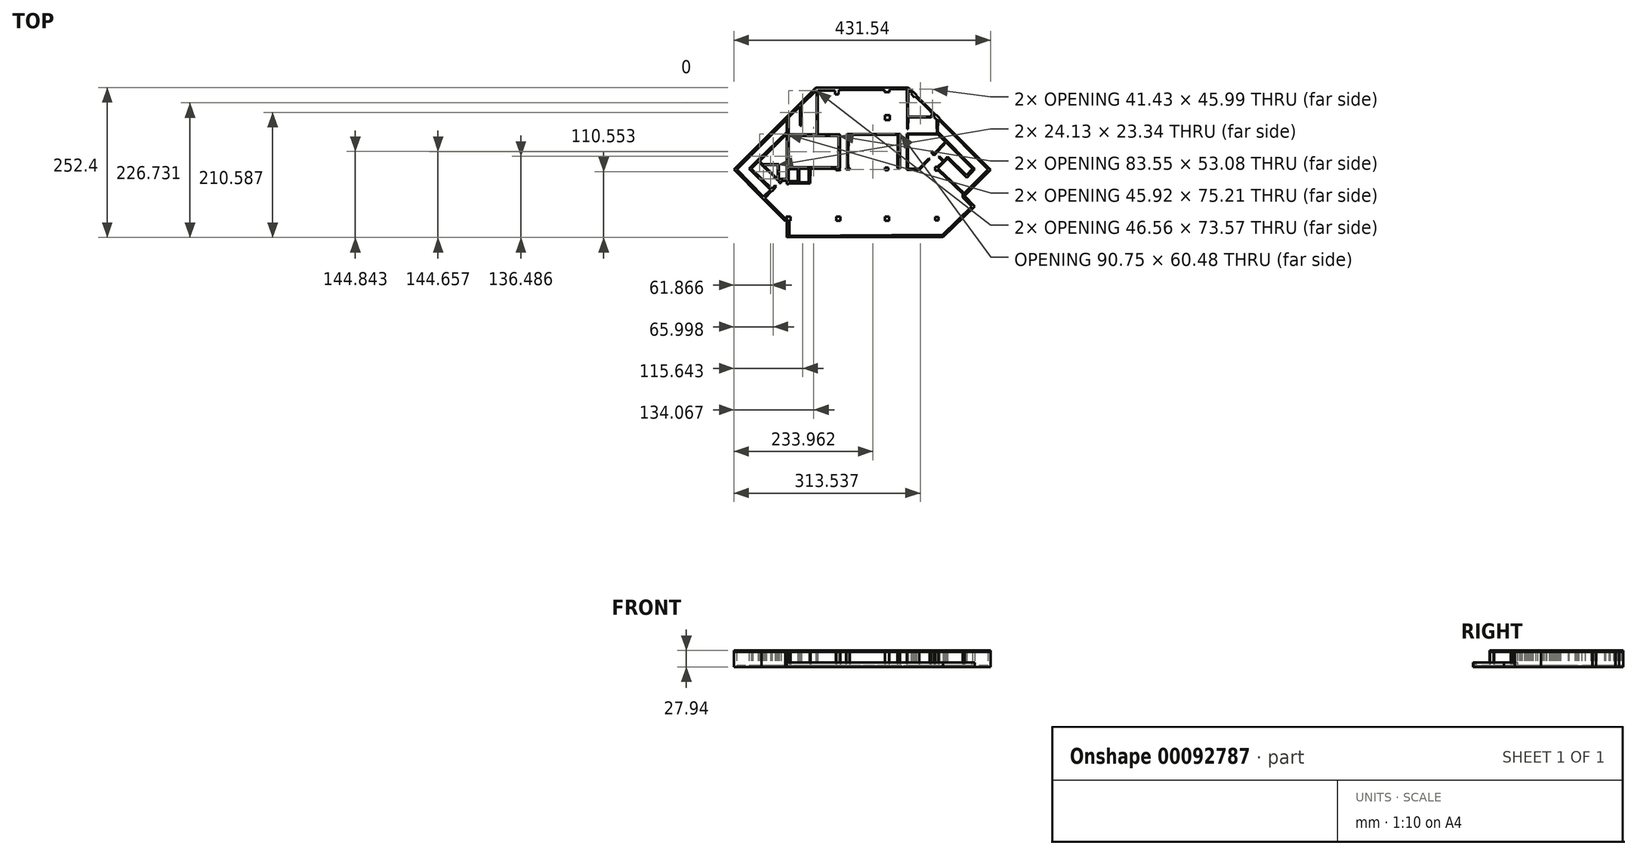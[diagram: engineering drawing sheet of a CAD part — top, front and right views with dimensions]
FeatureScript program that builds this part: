
annotation { "Feature Type Name" : "Feature", "Feature Type Description" : "" }
export const myFeature = defineFeature(function(context is Context, id is Id, definition is map)
    precondition{}
    {
        {
            var Q0;
            Q0=qCreatedBy(makeId("Top.planeOp"),FACE);
            var sketch = newSketch(context, id + "F0", { "sketchPlane" : qUnion([Q0])});
            skFitSpline(sketch, "E0", {"points": [v(-174.44, 1.7) * mm, v(-159.98, -12.91) * mm, v(-156, -16.03) * mm, v(-141.6, -30.7) * mm]});
            skLineSegment(sketch, "E1", {"start": v(-78.22, 126.2) * mm, "end": v(-126.81, 77.3) * mm});
            skLineSegment(sketch, "E2", {"start": v(-126.81, 77.3) * mm, "end": v(-126.8, 72.34) * mm});
            skLineSegment(sketch, "E3", {"start": v(-126.8, 72.34) * mm, "end": v(-126.81, 51.33) * mm});
            skLineSegment(sketch, "E4", {"start": v(-126.81, 51.33) * mm, "end": v(-175, 4.76) * mm});
            skLineSegment(sketch, "E5", {"start": v(-175, 4.76) * mm, "end": v(-190.1, -10.54) * mm});
            skLineSegment(sketch, "E6", {"start": v(-190.1, -10.54) * mm, "end": v(-154.22, -45.73) * mm});
            skLineSegment(sketch, "E7", {"start": v(-154.22, -45.73) * mm, "end": v(-166.17, -57.54) * mm});
            skLineSegment(sketch, "E8", {"start": v(-166.17, -57.54) * mm, "end": v(-211.21, -11.79) * mm});
            skLineSegment(sketch, "E9", {"start": v(-211.21, -11.79) * mm, "end": v(-186.84, 13.8) * mm});
            skLineSegment(sketch, "E10", {"start": v(-186.84, 13.8) * mm, "end": v(-184.08, 15.95) * mm});
            skLineSegment(sketch, "E11", {"start": v(-184.08, 15.95) * mm, "end": v(-126.84, 72.68) * mm});
            skLineSegment(sketch, "E12", {"start": v(-126.84, 72.68) * mm, "end": v(-126.9, 77.1) * mm});
            skLineSegment(sketch, "E13", {"start": v(-126.9, 77.1) * mm, "end": v(-215.77, -11.79) * mm});
            skLineSegment(sketch, "E14", {"start": v(-215.77, -11.79) * mm, "end": v(-169.23, -58.33) * mm});
            skLineSegment(sketch, "E15", {"start": v(-169.23, -58.33) * mm, "end": v(-169.38, -58.47) * mm});
            skLineSegment(sketch, "E16", {"start": v(-169.38, -58.47) * mm, "end": v(-129.39, -98.47) * mm});
            skLineSegment(sketch, "E17", {"start": v(-129.39, -98.47) * mm, "end": v(-126.88, -97.8) * mm});
            skLineSegment(sketch, "E18", {"start": v(-126.88, -97.8) * mm, "end": v(-126.88, -93.73) * mm});
            skLineSegment(sketch, "E19", {"start": v(-126.88, -93.73) * mm, "end": v(-130.37, -93.73) * mm});
            skLineSegment(sketch, "E20", {"start": v(-130.37, -93.73) * mm, "end": v(-161.45, -62.66) * mm});
            skLineSegment(sketch, "E21", {"start": v(-161.45, -62.66) * mm, "end": v(-163.98, -59.75) * mm});
            skLineSegment(sketch, "E22", {"start": v(-163.98, -59.75) * mm, "end": v(-152.34, -47.57) * mm});
            skLineSegment(sketch, "E23", {"start": v(-152.34, -47.57) * mm, "end": v(-151.65, -48.26) * mm});
            skLineSegment(sketch, "E24", {"start": v(-151.65, -48.26) * mm, "end": v(-144.6, -40.12) * mm});
            skLineSegment(sketch, "E25", {"start": v(-144.6, -40.12) * mm, "end": v(-146.73, -38.49) * mm});
            skLineSegment(sketch, "E26", {"start": v(-146.73, -38.49) * mm, "end": v(-151.97, -44.07) * mm});
            skLineSegment(sketch, "E27", {"start": v(-151.97, -44.07) * mm, "end": v(-186.58, -10.29) * mm});
            skLineSegment(sketch, "E28", {"start": v(-186.58, -10.29) * mm, "end": v(-174.44, 1.7) * mm});
            skFitSpline(sketch, "E29", {"points": [v(-39.3, -9.75) * mm, v(-39.04, -9.69) * mm, v(-38.8, -9.64) * mm, v(-38.58, -9.63) * mm]});
            skFitSpline(sketch, "E30", {"points": [v(-38.58, -9.63) * mm, v(-38.22, -9.61) * mm, v(-37.96, -9.73) * mm, v(-37.91, -10.14) * mm]});
            skFitSpline(sketch, "E31", {"points": [v(-37.91, -10.14) * mm, v(-37.56, -13.27) * mm, v(-37.75, -11.26) * mm, v(-37.91, -9.63) * mm]});
            skLineSegment(sketch, "E32", {"start": v(-141.6, -30.7) * mm, "end": v(-139.3, -30.6) * mm});
            skLineSegment(sketch, "E33", {"start": v(-139.3, -30.6) * mm, "end": v(-139.3, -34.5) * mm});
            skLineSegment(sketch, "E34", {"start": v(-139.3, -34.5) * mm, "end": v(-136.14, -34.74) * mm});
            skLineSegment(sketch, "E35", {"start": v(-136.14, -34.74) * mm, "end": v(-136.54, -30.6) * mm});
            skLineSegment(sketch, "E36", {"start": v(-136.54, -30.6) * mm, "end": v(-126.83, -30.6) * mm});
            skLineSegment(sketch, "E37", {"start": v(-126.83, -30.6) * mm, "end": v(-126.83, -36.33) * mm});
            skLineSegment(sketch, "E38", {"start": v(-126.83, -36.33) * mm, "end": v(-123.4, -36.33) * mm});
            skLineSegment(sketch, "E39", {"start": v(-123.4, -36.33) * mm, "end": v(-123.4, -35.16) * mm});
            skLineSegment(sketch, "E40", {"start": v(-123.4, -35.16) * mm, "end": v(-87.46, -35.4) * mm});
            skLineSegment(sketch, "E41", {"start": v(-87.46, -35.4) * mm, "end": v(-86.96, -10.29) * mm});
            skLineSegment(sketch, "E42", {"start": v(-86.96, -10.29) * mm, "end": v(-44.15, -10.22) * mm});
            skLineSegment(sketch, "E43", {"start": v(-44.15, -10.22) * mm, "end": v(-44.15, -12.64) * mm});
            skLineSegment(sketch, "E44", {"start": v(-44.15, -12.64) * mm, "end": v(-39.3, -12.64) * mm});
            skLineSegment(sketch, "E45", {"start": v(-39.3, -12.64) * mm, "end": v(-39.3, -9.75) * mm});
            skLineSegment(sketch, "E46", {"start": v(-37.91, -9.63) * mm, "end": v(-37.65, -9.63) * mm});
            skLineSegment(sketch, "E47", {"start": v(-37.65, -9.63) * mm, "end": v(-37.65, 47.6) * mm});
            skLineSegment(sketch, "E48", {"start": v(-37.65, 47.6) * mm, "end": v(-75.14, 47.6) * mm});
            skLineSegment(sketch, "E49", {"start": v(-75.14, 47.6) * mm, "end": v(-75.14, 121.17) * mm});
            skLineSegment(sketch, "E50", {"start": v(-75.14, 121.17) * mm, "end": v(-45.4, 121.17) * mm});
            skLineSegment(sketch, "E51", {"start": v(-45.4, 121.17) * mm, "end": v(-45.5, 114.54) * mm});
            skLineSegment(sketch, "E52", {"start": v(-45.5, 114.54) * mm, "end": v(-39.6, 114.51) * mm});
            skLineSegment(sketch, "E53", {"start": v(-39.6, 114.51) * mm, "end": v(-39.55, 122.46) * mm});
            skLineSegment(sketch, "E54", {"start": v(-39.55, 122.46) * mm, "end": v(-8.25, 122.35) * mm});
            skLineSegment(sketch, "E55", {"start": v(-8.25, 122.35) * mm, "end": v(-5.93, 122.35) * mm});
            skLineSegment(sketch, "E56", {"start": v(-5.93, 122.35) * mm, "end": v(37.67, 122.2) * mm});
            skLineSegment(sketch, "E57", {"start": v(37.67, 122.2) * mm, "end": v(37.67, 118.36) * mm});
            skLineSegment(sketch, "E58", {"start": v(37.67, 118.36) * mm, "end": v(46.1, 118.3) * mm});
            skLineSegment(sketch, "E59", {"start": v(46.1, 118.3) * mm, "end": v(46.09, 123.29) * mm});
            skLineSegment(sketch, "E60", {"start": v(46.09, 123.29) * mm, "end": v(75.25, 123.43) * mm});
            skLineSegment(sketch, "E61", {"start": v(75.25, 123.43) * mm, "end": v(75.16, 104.38) * mm});
            skLineSegment(sketch, "E62", {"start": v(75.16, 104.38) * mm, "end": v(75.4, 102.33) * mm});
            skLineSegment(sketch, "E63", {"start": v(75.4, 102.33) * mm, "end": v(75.46, 56.57) * mm});
            skLineSegment(sketch, "E64", {"start": v(75.46, 56.57) * mm, "end": v(77.18, 56.54) * mm});
            skLineSegment(sketch, "E65", {"start": v(77.18, 56.54) * mm, "end": v(77.26, 76) * mm});
            skLineSegment(sketch, "E66", {"start": v(77.26, 76) * mm, "end": v(115.98, 75.8) * mm});
            skLineSegment(sketch, "E67", {"start": v(115.98, 75.8) * mm, "end": v(119.9, 80.73) * mm});
            skLineSegment(sketch, "E68", {"start": v(118.48, 82.16) * mm, "end": v(114.54, 77.53) * mm});
            skLineSegment(sketch, "E69", {"start": v(114.54, 77.53) * mm, "end": v(77.05, 77.9) * mm});
            skLineSegment(sketch, "E70", {"start": v(77.05, 77.9) * mm, "end": v(77.47, 123.47) * mm});
            skLineSegment(sketch, "E71", {"start": v(77.47, 123.47) * mm, "end": v(77.64, 123.53) * mm});
            skLineSegment(sketch, "E72", {"start": v(77.64, 123.53) * mm, "end": v(83.03, 117.44) * mm});
            skLineSegment(sketch, "E73", {"start": v(83.03, 117.44) * mm, "end": v(84.34, 118.24) * mm});
            skLineSegment(sketch, "E74", {"start": v(85.11, 119.02) * mm, "end": v(77.54, 126.1) * mm});
            skLineSegment(sketch, "E75", {"start": v(77.54, 126.1) * mm, "end": v(46.08, 126.12) * mm});
            skLineSegment(sketch, "E76", {"start": v(46.08, 126.12) * mm, "end": v(37.67, 126.13) * mm});
            skLineSegment(sketch, "E77", {"start": v(37.67, 126.13) * mm, "end": v(-78.22, 126.2) * mm});
            skLineSegment(sketch, "E78", {"start": v(-77.1, 121.17) * mm, "end": v(-76.85, 121.17) * mm});
            skLineSegment(sketch, "E79", {"start": v(-76.85, 121.17) * mm, "end": v(-76.85, 47.6) * mm});
            skLineSegment(sketch, "E80", {"start": v(-76.85, 47.6) * mm, "end": v(-123.4, 47.6) * mm});
            skLineSegment(sketch, "E81", {"start": v(-123.4, 47.6) * mm, "end": v(-123.4, 76.02) * mm});
            skLineSegment(sketch, "E82", {"start": v(-123.4, 76.02) * mm, "end": v(-104.36, 94.6) * mm});
            skLineSegment(sketch, "E83", {"start": v(-104.36, 94.6) * mm, "end": v(-104.36, 62) * mm});
            skLineSegment(sketch, "E84", {"start": v(-104.36, 62) * mm, "end": v(-102.22, 62) * mm});
            skLineSegment(sketch, "E85", {"start": v(-102.22, 62) * mm, "end": v(-102.22, 96.68) * mm});
            skLineSegment(sketch, "E86", {"start": v(-102.22, 96.68) * mm, "end": v(-77.1, 121.17) * mm});
            skLineSegment(sketch, "E87", {"start": v(-126.81, 47.9) * mm, "end": v(-126.83, -27.32) * mm});
            skLineSegment(sketch, "E88", {"start": v(-126.83, -27.32) * mm, "end": v(-140.53, -27.32) * mm});
            skLineSegment(sketch, "E89", {"start": v(-140.53, -27.32) * mm, "end": v(-140.53, -2.97) * mm});
            skLineSegment(sketch, "E90", {"start": v(-140.53, -2.97) * mm, "end": v(-167.49, -2.87) * mm});
            skLineSegment(sketch, "E91", {"start": v(-167.49, -2.87) * mm, "end": v(-172.73, 2.5) * mm});
            skLineSegment(sketch, "E92", {"start": v(-172.73, 2.5) * mm, "end": v(-126.81, 47.9) * mm});
            skLineSegment(sketch, "E93", {"start": v(-123.4, 45) * mm, "end": v(-39.93, 45) * mm});
            skLineSegment(sketch, "E94", {"start": v(-39.93, 45) * mm, "end": v(-39.93, -7.8) * mm});
            skLineSegment(sketch, "E95", {"start": v(-39.93, -7.8) * mm, "end": v(-44.15, -7.8) * mm});
            skLineSegment(sketch, "E96", {"start": v(-44.15, -7.8) * mm, "end": v(-44.15, -7.96) * mm});
            skLineSegment(sketch, "E97", {"start": v(-44.15, -7.96) * mm, "end": v(-74.51, -7.99) * mm});
            skLineSegment(sketch, "E98", {"start": v(-74.51, -7.99) * mm, "end": v(-76.7, -8) * mm});
            skLineSegment(sketch, "E99", {"start": v(-76.7, -8) * mm, "end": v(-81.23, -8.01) * mm});
            skLineSegment(sketch, "E100", {"start": v(-81.23, -8.01) * mm, "end": v(-84.46, -8.02) * mm});
            skLineSegment(sketch, "E101", {"start": v(-84.46, -8.02) * mm, "end": v(-89.03, -8.04) * mm});
            skLineSegment(sketch, "E102", {"start": v(-89.03, -8.04) * mm, "end": v(-100.13, -8.08) * mm});
            skLineSegment(sketch, "E103", {"start": v(-100.13, -8.08) * mm, "end": v(-103.17, -8.08) * mm});
            skLineSegment(sketch, "E104", {"start": v(-103.17, -8.08) * mm, "end": v(-123.4, -8.08) * mm});
            skLineSegment(sketch, "E105", {"start": v(-123.4, -8.08) * mm, "end": v(-123.48, 18.17) * mm});
            skLineSegment(sketch, "E106", {"start": v(-123.48, 18.17) * mm, "end": v(-123.4, 20.8) * mm});
            skLineSegment(sketch, "E107", {"start": v(-123.4, 20.8) * mm, "end": v(-123.4, 43.14) * mm});
            skLineSegment(sketch, "E108", {"start": v(-123.4, 43.14) * mm, "end": v(-123.4, 45) * mm});
            skLineSegment(sketch, "E109", {"start": v(-165.97, -3.97) * mm, "end": v(-141.84, -4.18) * mm});
            skLineSegment(sketch, "E110", {"start": v(-141.84, -4.18) * mm, "end": v(-141.84, -27.32) * mm});
            skLineSegment(sketch, "E111", {"start": v(-141.84, -27.32) * mm, "end": v(-142.8, -27.32) * mm});
            skLineSegment(sketch, "E112", {"start": v(-142.8, -27.32) * mm, "end": v(-165.97, -3.97) * mm});
            skFitSpline(sketch, "E113", {"points": [v(-89.98, -33.22) * mm, v(-95.4, -33.13) * mm, v(-100.83, -33.2) * mm, v(-106.26, -33.23) * mm]});
            skLineSegment(sketch, "E114", {"start": v(-89.77, -10.64) * mm, "end": v(-89.98, -33.22) * mm});
            skLineSegment(sketch, "E115", {"start": v(-106.26, -33.23) * mm, "end": v(-106.16, -31.94) * mm});
            skLineSegment(sketch, "E116", {"start": v(-106.16, -31.94) * mm, "end": v(-106.16, -29.03) * mm});
            skLineSegment(sketch, "E117", {"start": v(-106.16, -29.03) * mm, "end": v(-106.16, -18.64) * mm});
            skLineSegment(sketch, "E118", {"start": v(-106.16, -18.64) * mm, "end": v(-106.16, -10.8) * mm});
            skLineSegment(sketch, "E119", {"start": v(-106.16, -10.8) * mm, "end": v(-104.16, -10.8) * mm});
            skLineSegment(sketch, "E120", {"start": v(-104.16, -10.8) * mm, "end": v(-89.77, -10.64) * mm});
            skLineSegment(sketch, "E121", {"start": v(-123.4, -10.8) * mm, "end": v(-108.22, -10.8) * mm});
            skLineSegment(sketch, "E122", {"start": v(-108.22, -10.8) * mm, "end": v(-108.22, -17.72) * mm});
            skLineSegment(sketch, "E123", {"start": v(-108.22, -17.72) * mm, "end": v(-108.43, -28.83) * mm});
            skLineSegment(sketch, "E124", {"start": v(-108.43, -28.83) * mm, "end": v(-108.4, -31.6) * mm});
            skLineSegment(sketch, "E125", {"start": v(-108.4, -31.6) * mm, "end": v(-123.4, -31.6) * mm});
            skLineSegment(sketch, "E126", {"start": v(-123.4, -31.6) * mm, "end": v(-123.4, -10.8) * mm});
            skFitSpline(sketch, "E127", {"points": [v(125.51, 71.94) * mm, v(125.5, 71.02) * mm, v(125.56, 51.87) * mm, v(125.52, 49.04) * mm]});
            skLineSegment(sketch, "E128", {"start": v(127.2, 50.6) * mm, "end": v(127.44, 71.54) * mm});
            skLineSegment(sketch, "E129", {"start": v(130.47, 74.56) * mm, "end": v(124.33, 80.7) * mm});
            skLineSegment(sketch, "E130", {"start": v(124.33, 80.7) * mm, "end": v(123.68, 80.04) * mm});
            skLineSegment(sketch, "E131", {"start": v(123.68, 80.04) * mm, "end": v(91.07, 112.71) * mm});
            skLineSegment(sketch, "E132", {"start": v(89.6, 111.23) * mm, "end": v(108.47, 92.23) * mm});
            skLineSegment(sketch, "E133", {"start": v(108.47, 92.23) * mm, "end": v(109.78, 90.91) * mm});
            skLineSegment(sketch, "E134", {"start": v(109.78, 90.91) * mm, "end": v(122.13, 78.49) * mm});
            skLineSegment(sketch, "E135", {"start": v(122.13, 78.49) * mm, "end": v(120.55, 76.9) * mm});
            skLineSegment(sketch, "E136", {"start": v(120.55, 76.9) * mm, "end": v(125.51, 71.94) * mm});
            skLineSegment(sketch, "E137", {"start": v(74.72, -12.3) * mm, "end": v(95.78, -12.4) * mm});
            skLineSegment(sketch, "E138", {"start": v(112.04, 6.96) * mm, "end": v(95.18, -10.18) * mm});
            skLineSegment(sketch, "E139", {"start": v(127.16, 47.53) * mm, "end": v(139.53, 34.97) * mm});
            skLineSegment(sketch, "E140", {"start": v(139.53, 34.97) * mm, "end": v(120.79, 15.01) * mm});
            skLineSegment(sketch, "E141", {"start": v(120.79, 15.01) * mm, "end": v(116.76, 19.45) * mm});
            skLineSegment(sketch, "E142", {"start": v(141.14, 33.76) * mm, "end": v(185.7, -10.58) * mm});
            skLineSegment(sketch, "E143", {"start": v(185.7, -10.58) * mm, "end": v(175.09, -21.2) * mm});
            skLineSegment(sketch, "E144", {"start": v(175.09, -21.2) * mm, "end": v(143.8, 9.63) * mm});
            skLineSegment(sketch, "E145", {"start": v(143.8, 9.63) * mm, "end": v(137.11, 3.07) * mm});
            skLineSegment(sketch, "E146", {"start": v(137.11, 3.07) * mm, "end": v(129.7, 10.9) * mm});
            skLineSegment(sketch, "E147", {"start": v(129.7, 10.9) * mm, "end": v(128.05, 9.25) * mm});
            skLineSegment(sketch, "E148", {"start": v(128.05, 9.25) * mm, "end": v(135.73, 1.71) * mm});
            skLineSegment(sketch, "E149", {"start": v(135.73, 1.71) * mm, "end": v(126.64, -7.2) * mm});
            skLineSegment(sketch, "E150", {"start": v(211.43, -11.5) * mm, "end": v(171.6, -51.7) * mm});
            skLineSegment(sketch, "E151", {"start": v(168.9, -58.57) * mm, "end": v(184.2, -73.68) * mm});
            skLineSegment(sketch, "E152", {"start": v(184.2, -73.68) * mm, "end": v(135.65, -121.55) * mm});
            skLineSegment(sketch, "E153", {"start": v(135.65, -121.55) * mm, "end": v(-122.43, -123.18) * mm});
            skLineSegment(sketch, "E154", {"start": v(-122.43, -123.18) * mm, "end": v(-122.62, -97.68) * mm});
            skLineSegment(sketch, "E155", {"start": v(-122.62, -97.68) * mm, "end": v(-126.8, -98.21) * mm});
            skLineSegment(sketch, "E156", {"start": v(-126.8, -98.21) * mm, "end": v(-126.83, -126.2) * mm});
            skLineSegment(sketch, "E157", {"start": v(-126.83, -126.2) * mm, "end": v(136.25, -125.48) * mm});
            skLineSegment(sketch, "E158", {"start": v(136.25, -125.48) * mm, "end": v(189.43, -74.06) * mm});
            skLineSegment(sketch, "E159", {"start": v(189.43, -74.06) * mm, "end": v(172.25, -55.86) * mm});
            skLineSegment(sketch, "E160", {"start": v(172.25, -55.86) * mm, "end": v(215.77, -12.25) * mm});
            skLineSegment(sketch, "E161", {"start": v(128.41, -8.2) * mm, "end": v(143.43, 6.7) * mm});
            skLineSegment(sketch, "E162", {"start": v(38.48, 79.58) * mm, "end": v(46.54, 79.58) * mm});
            skLineSegment(sketch, "E163", {"start": v(46.54, 79.58) * mm, "end": v(46.54, 71.52) * mm});
            skLineSegment(sketch, "E164", {"start": v(46.54, 71.52) * mm, "end": v(38.48, 71.52) * mm});
            skLineSegment(sketch, "E165", {"start": v(38.48, 71.52) * mm, "end": v(38.48, 79.58) * mm});
            skLineSegment(sketch, "E166", {"start": v(38.47, -8.7) * mm, "end": v(43.93, -8.7) * mm});
            skLineSegment(sketch, "E167", {"start": v(43.93, -8.7) * mm, "end": v(43.93, -13.16) * mm});
            skLineSegment(sketch, "E168", {"start": v(43.93, -13.16) * mm, "end": v(38.47, -13.16) * mm});
            skLineSegment(sketch, "E169", {"start": v(38.47, -13.16) * mm, "end": v(38.47, -8.7) * mm});
            skLineSegment(sketch, "E170", {"start": v(85.56, 119.47) * mm, "end": v(91.7, 113.34) * mm});
            skLineSegment(sketch, "E171", {"start": v(91.7, 113.34) * mm, "end": v(87.9, 109.55) * mm});
            skLineSegment(sketch, "E172", {"start": v(87.9, 109.55) * mm, "end": v(81.77, 115.68) * mm});
            skLineSegment(sketch, "E173", {"start": v(81.77, 115.68) * mm, "end": v(85.56, 119.47) * mm});
            skLineSegment(sketch, "E174", {"start": v(-43.92, -90.8) * mm, "end": v(-36.51, -90.8) * mm});
            skLineSegment(sketch, "E175", {"start": v(-36.51, -90.8) * mm, "end": v(-36.51, -98.22) * mm});
            skLineSegment(sketch, "E176", {"start": v(-36.51, -98.22) * mm, "end": v(-43.92, -98.22) * mm});
            skLineSegment(sketch, "E177", {"start": v(-43.92, -98.22) * mm, "end": v(-43.92, -90.8) * mm});
            skLineSegment(sketch, "E178", {"start": v(37.9, -90.8) * mm, "end": v(45.3, -90.8) * mm});
            skLineSegment(sketch, "E179", {"start": v(45.3, -90.8) * mm, "end": v(45.3, -98.22) * mm});
            skLineSegment(sketch, "E180", {"start": v(45.3, -98.22) * mm, "end": v(37.9, -98.22) * mm});
            skLineSegment(sketch, "E181", {"start": v(37.9, -98.22) * mm, "end": v(37.9, -90.8) * mm});
            skLineSegment(sketch, "E182", {"start": v(-128.02, -90.8) * mm, "end": v(-120.61, -90.8) * mm});
            skLineSegment(sketch, "E183", {"start": v(-120.61, -90.8) * mm, "end": v(-120.61, -98.22) * mm});
            skLineSegment(sketch, "E184", {"start": v(-120.61, -98.22) * mm, "end": v(-128.02, -98.22) * mm});
            skLineSegment(sketch, "E185", {"start": v(-128.02, -98.22) * mm, "end": v(-128.02, -90.8) * mm});
            skLineSegment(sketch, "E186", {"start": v(122.42, -7.2) * mm, "end": v(128.41, -7.2) * mm});
            skLineSegment(sketch, "E187", {"start": v(128.41, -7.2) * mm, "end": v(128.41, -8.2) * mm});
            skLineSegment(sketch, "E188", {"start": v(128.41, -13.34) * mm, "end": v(122.42, -13.34) * mm});
            skLineSegment(sketch, "E189", {"start": v(122.42, -13.34) * mm, "end": v(122.42, -7.2) * mm});
            skLineSegment(sketch, "E190", {"start": v(122.42, -91.47) * mm, "end": v(128.41, -91.47) * mm});
            skLineSegment(sketch, "E191", {"start": v(128.41, -91.47) * mm, "end": v(128.41, -97.6) * mm});
            skLineSegment(sketch, "E192", {"start": v(128.41, -97.6) * mm, "end": v(122.42, -97.6) * mm});
            skLineSegment(sketch, "E193", {"start": v(122.42, -97.6) * mm, "end": v(122.42, -91.47) * mm});
            skFitSpline(sketch, "E194", {"points": [v(-23.35, -8.97) * mm, v(-24.15, 7.44) * mm, v(-23.1, 27.52) * mm, v(-22.95, 45.86) * mm]});
            skLineSegment(sketch, "E195", {"start": v(63.33, 48.88) * mm, "end": v(-25.57, 48.08) * mm});
            skLineSegment(sketch, "E196", {"start": v(-25.57, 48.08) * mm, "end": v(-25.57, -8.97) * mm});
            skLineSegment(sketch, "E197", {"start": v(-25.57, -8.97) * mm, "end": v(-27.13, -8.97) * mm});
            skLineSegment(sketch, "E198", {"start": v(-27.13, -8.97) * mm, "end": v(-27.18, -11.6) * mm});
            skLineSegment(sketch, "E199", {"start": v(-27.18, -11.6) * mm, "end": v(-20.78, -11.6) * mm});
            skLineSegment(sketch, "E200", {"start": v(-20.78, -11.6) * mm, "end": v(-20.78, -8.97) * mm});
            skLineSegment(sketch, "E201", {"start": v(-20.78, -8.97) * mm, "end": v(-23.35, -8.97) * mm});
            skLineSegment(sketch, "E202", {"start": v(-22.95, 45.86) * mm, "end": v(59.85, 46.52) * mm});
            skLineSegment(sketch, "E203", {"start": v(59.85, 46.52) * mm, "end": v(59.34, -9.83) * mm});
            skLineSegment(sketch, "E204", {"start": v(59.34, -9.83) * mm, "end": v(63.57, -10.08) * mm});
            skLineSegment(sketch, "E205", {"start": v(63.57, -10.08) * mm, "end": v(63.33, 48.88) * mm});
            skLineSegment(sketch, "E206", {"start": v(130.47, 74.56) * mm, "end": v(127.44, 71.54) * mm});
            skLineSegment(sketch, "E207", {"start": v(125.51, 71.94) * mm, "end": v(127.44, 71.54) * mm});
            skLineSegment(sketch, "E208", {"start": v(211.43, -11.5) * mm, "end": v(128.33, 72.43) * mm});
            skLineSegment(sketch, "E209", {"start": v(215.77, -12.25) * mm, "end": v(129.84, 73.93) * mm});
            skLineSegment(sketch, "E210", {"start": v(127.2, 50.6) * mm, "end": v(127.16, 47.53) * mm});
            skLineSegment(sketch, "E211", {"start": v(125.52, 49.04) * mm, "end": v(75.32, 48.99) * mm});
            skLineSegment(sketch, "E212", {"start": v(127.16, 47.53) * mm, "end": v(77.1, 47.48) * mm});
            skLineSegment(sketch, "E213", {"start": v(77.1, 47.48) * mm, "end": v(77.1, -10.18) * mm});
            skLineSegment(sketch, "E214", {"start": v(77.1, -10.18) * mm, "end": v(95.18, -10.18) * mm});
            skLineSegment(sketch, "E215", {"start": v(74.72, -12.3) * mm, "end": v(75.32, 48.99) * mm});
            skLineSegment(sketch, "E216", {"start": v(77.1, 47.48) * mm, "end": v(75.32, 48.99) * mm});
            skLineSegment(sketch, "E217", {"start": v(95.78, -12.4) * mm, "end": v(113.8, 5.92) * mm});
            skLineSegment(sketch, "E218", {"start": v(113.8, 5.92) * mm, "end": v(112.04, 6.96) * mm});
            skLineSegment(sketch, "E219", {"start": v(141.14, 33.76) * mm, "end": v(120.79, 12.09) * mm});
            skLineSegment(sketch, "E220", {"start": v(120.79, 12.09) * mm, "end": v(115.6, 17.8) * mm});
            skLineSegment(sketch, "E221", {"start": v(115.6, 17.8) * mm, "end": v(116.76, 19.45) * mm});
            skLineSegment(sketch, "E222", {"start": v(139.53, 34.97) * mm, "end": v(141.14, 33.76) * mm});
            skLineSegment(sketch, "E223", {"start": v(189.32, -11.19) * mm, "end": v(127.2, 51.55) * mm});
            skLineSegment(sketch, "E224", {"start": v(127.2, 51.55) * mm, "end": v(127.16, 47.53) * mm});
            skLineSegment(sketch, "E225", {"start": v(143.43, 6.7) * mm, "end": v(175.69, -25.77) * mm});
            skLineSegment(sketch, "E226", {"start": v(175.69, -25.77) * mm, "end": v(189.32, -11.19) * mm});
            skLineSegment(sketch, "E227", {"start": v(185.7, -10.58) * mm, "end": v(189.32, -11.19) * mm});
            skPoint(sketch, "E228.orphan", {"position": v(128.41, -13.34) * mm});
            skLineSegment(sketch, "E229", {"start": v(128.41, -8.2) * mm, "end": v(128.41, -13.34) * mm});
            skLineSegment(sketch, "E230", {"start": v(168.9, -52) * mm, "end": v(168.9, -58.57) * mm});
            skLineSegment(sketch, "E231", {"start": v(172.25, -55.86) * mm, "end": v(171.6, -51.7) * mm});
            skLineSegment(sketch, "E232", {"start": v(171.6, -51.7) * mm, "end": v(168.9, -52) * mm});
            skLineSegment(sketch, "E233", {"start": v(128.41, -13.34) * mm, "end": v(168.9, -52) * mm});
            skLineSegment(sketch, "E234", {"start": v(171.6, -51.7) * mm, "end": v(128.41, -10.77) * mm});
            skLineSegment(sketch, "E235", {"start": v(128.41, -10.77) * mm, "end": v(128.41, -13.34) * mm});
            skSolve(sketch);
        }
        {
            var Q0;
            Q0=makeQuery(id+"F0.imprint","IMPRINT",FACE,{"disambiguationData":[TD([[makeQuery(id+"F0.imprint","IMPRINT",EDGE,{"derivedFrom":sQuery(id+"F0.wireOp",EDGE,"E0")}),1.0]])]});
            var Q1;
            {var subQ9=sQuery(id+"F0.wireOp",EDGE,"E18");Q1=makeQuery(id+"F0.imprint","IMPRINT",FACE,{"disambiguationData":[TD([[makeQuery(id+"F0.imprint","IMPRINT",EDGE,{"derivedFrom":subQ9}),-1.0]])]});}
            var Q2;
            Q2=makeQuery(id+"F0.imprint","IMPRINT",FACE,{"disambiguationData":[TD([[makeQuery(id+"F0.imprint","IMPRINT",EDGE,{"derivedFrom":sQuery(id+"F0.wireOp",EDGE,"E174")}),-1.0]])]});
            var Q3;
            Q3=makeQuery(id+"F0.imprint","IMPRINT",FACE,{"disambiguationData":[TD([[makeQuery(id+"F0.imprint","IMPRINT",EDGE,{"derivedFrom":sQuery(id+"F0.wireOp",EDGE,"E178")}),-1.0]])]});
            var Q4;
            Q4=makeQuery(id+"F0.imprint","IMPRINT",FACE,{"disambiguationData":[TD([[makeQuery(id+"F0.imprint","IMPRINT",EDGE,{"derivedFrom":sQuery(id+"F0.wireOp",EDGE,"E190")}),-1.0]])]});
            var Q5;
            {var subQ8=sQuery(id+"F0.wireOp",EDGE,"E188");Q5=makeQuery(id+"F0.imprint","IMPRINT",FACE,{"disambiguationData":[TD([[makeQuery(id+"F0.imprint","IMPRINT",EDGE,{"derivedFrom":subQ8}),-1.0]])]});}
            var Q6;
            Q6=makeQuery(id+"F0.imprint","IMPRINT",FACE,{"disambiguationData":[TD([[makeQuery(id+"F0.imprint","IMPRINT",EDGE,{"derivedFrom":sQuery(id+"F0.wireOp",EDGE,"E166")}),-1.0]])]});
            var Q7;
            Q7=makeQuery(id+"F0.imprint","IMPRINT",FACE,{"disambiguationData":[TD([[makeQuery(id+"F0.imprint","IMPRINT",EDGE,{"derivedFrom":sQuery(id+"F0.wireOp",EDGE,"E162")}),-1.0]])]});
            var Q8;
            Q8=makeQuery(id+"F0.imprint","IMPRINT",FACE,{"disambiguationData":[TD([[makeQuery(id+"F0.imprint","IMPRINT",EDGE,{"derivedFrom":sQuery(id+"F0.wireOp",EDGE,"E194")}),1.0]])]});
            var Q9;
            {var subQ7=sQuery(id+"F0.wireOp",EDGE,"E170");Q9=makeQuery(id+"F0.imprint","IMPRINT",FACE,{"disambiguationData":[TD([[makeQuery(id+"F0.imprint","IMPRINT",EDGE,{"derivedFrom":subQ7}),-1.0]])]});}
            var Q10;
            Q10=makeQuery(id+"F0.imprint","IMPRINT",FACE,{"disambiguationData":[TD([[makeQuery(id+"F0.imprint","IMPRINT",EDGE,{"derivedFrom":sQuery(id+"F0.wireOp",EDGE,"E129")}),1.0]])]});
            var Q11;
            Q11=makeQuery(id+"F0.imprint","IMPRINT",FACE,{"disambiguationData":[TD([[makeQuery(id+"F0.imprint","IMPRINT",EDGE,{"derivedFrom":sQuery(id+"F0.wireOp",EDGE,"E150")}),1.0]])]});
            var Q12;
            Q12=makeQuery(id+"F0.imprint","IMPRINT",FACE,{"disambiguationData":[TD([[makeQuery(id+"F0.imprint","IMPRINT",EDGE,{"derivedFrom":sQuery(id+"F0.wireOp",EDGE,"E127")}),1.0]])]});
            var Q13;
            Q13=makeQuery(id+"F0.imprint","IMPRINT",FACE,{"disambiguationData":[TD([[makeQuery(id+"F0.imprint","IMPRINT",EDGE,{"derivedFrom":sQuery(id+"F0.wireOp",EDGE,"E137")}),1.0]])]});
            var Q14;
            Q14=makeQuery(id+"F0.imprint","IMPRINT",FACE,{"disambiguationData":[TD([[makeQuery(id+"F0.imprint","IMPRINT",EDGE,{"derivedFrom":sQuery(id+"F0.wireOp",EDGE,"E140")}),1.0]])]});
            var Q15;
            Q15=makeQuery(id+"F0.imprint","IMPRINT",FACE,{"disambiguationData":[TD([[makeQuery(id+"F0.imprint","IMPRINT",EDGE,{"derivedFrom":sQuery(id+"F0.wireOp",EDGE,"E139")}),1.0]])]});
            var Q16;
            Q16=makeQuery(id+"F0.imprint","IMPRINT",FACE,{"disambiguationData":[TD([[makeQuery(id+"F0.imprint","IMPRINT",EDGE,{"derivedFrom":sQuery(id+"F0.wireOp",EDGE,"E143")}),1.0]])]});
            var Q17;
            Q17=makeQuery(id+"F0.imprint","IMPRINT",FACE,{"disambiguationData":[TD([[makeQuery(id+"F0.imprint","IMPRINT",EDGE,{"derivedFrom":sQuery(id+"F0.wireOp",EDGE,"E232")}),-1.0]])]});
            extrude(context, id + "F1", {"entities" : qUnion([Q0, Q1, Q2, Q3, Q4, Q5, Q6, Q7, Q8, Q9, Q10, Q11, Q12, Q13, Q14, Q15, Q16, Q17]), "depth" : 25.4 * mm});
        }
        {
            var Q0;
            Q0=makeQuery(id+"F0.imprint","IMPRINT",FACE,{"disambiguationData":[TD([[makeQuery(id+"F0.imprint","IMPRINT",EDGE,{"derivedFrom":sQuery(id+"F0.wireOp",EDGE,"E151")}),1.0]])]});
            extrude(context, id + "F2", {"entities" : qUnion([Q0]), "depth" : 7.62 * mm});
        }
        {
            var Q0;
            Q0=makeQuery(id+"F0.imprint","IMPRINT",FACE,{"disambiguationData":[TD([[makeQuery(id+"F0.imprint","IMPRINT",EDGE,{"derivedFrom":sQuery(id+"F0.wireOp",EDGE,"E0")}),-1.0]])]});
            var Q1;
            Q1=makeQuery(id+"F0.imprint","IMPRINT",FACE,{"disambiguationData":[TD([[makeQuery(id+"F0.imprint","IMPRINT",EDGE,{"derivedFrom":sQuery(id+"F0.wireOp",EDGE,"E113")}),-1.0]])]});
            var Q2;
            Q2=makeQuery(id+"F0.imprint","IMPRINT",FACE,{"disambiguationData":[TD([[makeQuery(id+"F0.imprint","IMPRINT",EDGE,{"derivedFrom":sQuery(id+"F0.wireOp",EDGE,"E93")}),-1.0]])]});
            var Q3;
            Q3=makeQuery(id+"F0.imprint","IMPRINT",FACE,{"disambiguationData":[TD([[makeQuery(id+"F0.imprint","IMPRINT",EDGE,{"derivedFrom":sQuery(id+"F0.wireOp",EDGE,"E78")}),-1.0]])]});
            var Q4;
            Q4=makeQuery(id+"F0.imprint","IMPRINT",FACE,{"disambiguationData":[TD([[makeQuery(id+"F0.imprint","IMPRINT",EDGE,{"derivedFrom":sQuery(id+"F0.wireOp",EDGE,"E87")}),-1.0]])]});
            var Q5;
            Q5=makeQuery(id+"F0.imprint","IMPRINT",FACE,{"disambiguationData":[TD([[makeQuery(id+"F0.imprint","IMPRINT",EDGE,{"derivedFrom":sQuery(id+"F0.wireOp",EDGE,"E109")}),-1.0]])]});
            var Q6;
            Q6=makeQuery(id+"F1.opExtrude","CAP_FACE",FACE,{"disambiguationData":[OSD([sQuery(id+"F0.wireOp",EDGE,"E0"),sQuery(id+"F0.wireOp",EDGE,"E1"),sQuery(id+"F0.wireOp",EDGE,"E2"),sQuery(id+"F0.wireOp",EDGE,"E3"),sQuery(id+"F0.wireOp",EDGE,"E4"),sQuery(id+"F0.wireOp",EDGE,"E5"),sQuery(id+"F0.wireOp",EDGE,"E6"),sQuery(id+"F0.wireOp",EDGE,"E7"),sQuery(id+"F0.wireOp",EDGE,"E8"),sQuery(id+"F0.wireOp",EDGE,"E9"),sQuery(id+"F0.wireOp",EDGE,"E10"),sQuery(id+"F0.wireOp",EDGE,"E11"),sQuery(id+"F0.wireOp",EDGE,"E12"),sQuery(id+"F0.wireOp",EDGE,"E13"),sQuery(id+"F0.wireOp",EDGE,"E14"),sQuery(id+"F0.wireOp",EDGE,"E15"),sQuery(id+"F0.wireOp",EDGE,"E16"),sQuery(id+"F0.wireOp",EDGE,"E17"),sQuery(id+"F0.wireOp",EDGE,"E19"),sQuery(id+"F0.wireOp",EDGE,"E20"),sQuery(id+"F0.wireOp",EDGE,"E21"),sQuery(id+"F0.wireOp",EDGE,"E22"),sQuery(id+"F0.wireOp",EDGE,"E23"),sQuery(id+"F0.wireOp",EDGE,"E24"),sQuery(id+"F0.wireOp",EDGE,"E25"),sQuery(id+"F0.wireOp",EDGE,"E26"),sQuery(id+"F0.wireOp",EDGE,"E27"),sQuery(id+"F0.wireOp",EDGE,"E28"),sQuery(id+"F0.wireOp",EDGE,"E29"),sQuery(id+"F0.wireOp",EDGE,"E30"),sQuery(id+"F0.wireOp",EDGE,"E31"),sQuery(id+"F0.wireOp",EDGE,"E32"),sQuery(id+"F0.wireOp",EDGE,"E33"),sQuery(id+"F0.wireOp",EDGE,"E34"),sQuery(id+"F0.wireOp",EDGE,"E35"),sQuery(id+"F0.wireOp",EDGE,"E36"),sQuery(id+"F0.wireOp",EDGE,"E37"),sQuery(id+"F0.wireOp",EDGE,"E38"),sQuery(id+"F0.wireOp",EDGE,"E39"),sQuery(id+"F0.wireOp",EDGE,"E40"),sQuery(id+"F0.wireOp",EDGE,"E41"),sQuery(id+"F0.wireOp",EDGE,"E42"),sQuery(id+"F0.wireOp",EDGE,"E43"),sQuery(id+"F0.wireOp",EDGE,"E44"),sQuery(id+"F0.wireOp",EDGE,"E45"),sQuery(id+"F0.wireOp",EDGE,"E46"),sQuery(id+"F0.wireOp",EDGE,"E47"),sQuery(id+"F0.wireOp",EDGE,"E48"),sQuery(id+"F0.wireOp",EDGE,"E49"),sQuery(id+"F0.wireOp",EDGE,"E50"),sQuery(id+"F0.wireOp",EDGE,"E51"),sQuery(id+"F0.wireOp",EDGE,"E52"),sQuery(id+"F0.wireOp",EDGE,"E53"),sQuery(id+"F0.wireOp",EDGE,"E54"),sQuery(id+"F0.wireOp",EDGE,"E55"),sQuery(id+"F0.wireOp",EDGE,"E56"),sQuery(id+"F0.wireOp",EDGE,"E57"),sQuery(id+"F0.wireOp",EDGE,"E58"),sQuery(id+"F0.wireOp",EDGE,"E59"),sQuery(id+"F0.wireOp",EDGE,"E60"),sQuery(id+"F0.wireOp",EDGE,"E61"),sQuery(id+"F0.wireOp",EDGE,"E62"),sQuery(id+"F0.wireOp",EDGE,"E63"),sQuery(id+"F0.wireOp",EDGE,"E64"),sQuery(id+"F0.wireOp",EDGE,"E65"),sQuery(id+"F0.wireOp",EDGE,"E66"),sQuery(id+"F0.wireOp",EDGE,"E67"),sQuery(id+"F0.wireOp",EDGE,"E68"),sQuery(id+"F0.wireOp",EDGE,"E69"),sQuery(id+"F0.wireOp",EDGE,"E70"),sQuery(id+"F0.wireOp",EDGE,"E71"),sQuery(id+"F0.wireOp",EDGE,"E72"),sQuery(id+"F0.wireOp",EDGE,"E73"),sQuery(id+"F0.wireOp",EDGE,"E74"),sQuery(id+"F0.wireOp",EDGE,"E75"),sQuery(id+"F0.wireOp",EDGE,"E76"),sQuery(id+"F0.wireOp",EDGE,"E77"),sQuery(id+"F0.wireOp",EDGE,"E78"),sQuery(id+"F0.wireOp",EDGE,"E79"),sQuery(id+"F0.wireOp",EDGE,"E80"),sQuery(id+"F0.wireOp",EDGE,"E81"),sQuery(id+"F0.wireOp",EDGE,"E82"),sQuery(id+"F0.wireOp",EDGE,"E83"),sQuery(id+"F0.wireOp",EDGE,"E84"),sQuery(id+"F0.wireOp",EDGE,"E85"),sQuery(id+"F0.wireOp",EDGE,"E86"),sQuery(id+"F0.wireOp",EDGE,"E87"),sQuery(id+"F0.wireOp",EDGE,"E88"),sQuery(id+"F0.wireOp",EDGE,"E89"),sQuery(id+"F0.wireOp",EDGE,"E90"),sQuery(id+"F0.wireOp",EDGE,"E91"),sQuery(id+"F0.wireOp",EDGE,"E92"),sQuery(id+"F0.wireOp",EDGE,"E93"),sQuery(id+"F0.wireOp",EDGE,"E94"),sQuery(id+"F0.wireOp",EDGE,"E95"),sQuery(id+"F0.wireOp",EDGE,"E96"),sQuery(id+"F0.wireOp",EDGE,"E97"),sQuery(id+"F0.wireOp",EDGE,"E98"),sQuery(id+"F0.wireOp",EDGE,"E99"),sQuery(id+"F0.wireOp",EDGE,"E100"),sQuery(id+"F0.wireOp",EDGE,"E101"),sQuery(id+"F0.wireOp",EDGE,"E102"),sQuery(id+"F0.wireOp",EDGE,"E103"),sQuery(id+"F0.wireOp",EDGE,"E104"),sQuery(id+"F0.wireOp",EDGE,"E105"),sQuery(id+"F0.wireOp",EDGE,"E106"),sQuery(id+"F0.wireOp",EDGE,"E107"),sQuery(id+"F0.wireOp",EDGE,"E108"),sQuery(id+"F0.wireOp",EDGE,"E109"),sQuery(id+"F0.wireOp",EDGE,"E110"),sQuery(id+"F0.wireOp",EDGE,"E111"),sQuery(id+"F0.wireOp",EDGE,"E112"),sQuery(id+"F0.wireOp",EDGE,"E113"),sQuery(id+"F0.wireOp",EDGE,"E114"),sQuery(id+"F0.wireOp",EDGE,"E115"),sQuery(id+"F0.wireOp",EDGE,"E116"),sQuery(id+"F0.wireOp",EDGE,"E117"),sQuery(id+"F0.wireOp",EDGE,"E118"),sQuery(id+"F0.wireOp",EDGE,"E119"),sQuery(id+"F0.wireOp",EDGE,"E120"),sQuery(id+"F0.wireOp",EDGE,"E121"),sQuery(id+"F0.wireOp",EDGE,"E122"),sQuery(id+"F0.wireOp",EDGE,"E123"),sQuery(id+"F0.wireOp",EDGE,"E124"),sQuery(id+"F0.wireOp",EDGE,"E125"),sQuery(id+"F0.wireOp",EDGE,"E126"),sQuery(id+"F0.wireOp",EDGE,"E127"),sQuery(id+"F0.wireOp",EDGE,"E128"),sQuery(id+"F0.wireOp",EDGE,"E129"),sQuery(id+"F0.wireOp",EDGE,"E130"),sQuery(id+"F0.wireOp",EDGE,"E131"),sQuery(id+"F0.wireOp",EDGE,"E132"),sQuery(id+"F0.wireOp",EDGE,"E133"),sQuery(id+"F0.wireOp",EDGE,"E134"),sQuery(id+"F0.wireOp",EDGE,"E135"),sQuery(id+"F0.wireOp",EDGE,"E136"),sQuery(id+"F0.wireOp",EDGE,"E137"),sQuery(id+"F0.wireOp",EDGE,"E138"),sQuery(id+"F0.wireOp",EDGE,"E150"),sQuery(id+"F0.wireOp",EDGE,"E160"),sQuery(id+"F0.wireOp",EDGE,"E170"),sQuery(id+"F0.wireOp",EDGE,"E171"),sQuery(id+"F0.wireOp",EDGE,"E172"),sQuery(id+"F0.wireOp",EDGE,"E173"),sQuery(id+"F0.wireOp",EDGE,"E185"),sQuery(id+"F0.wireOp",EDGE,"E206"),sQuery(id+"F0.wireOp",EDGE,"E208"),sQuery(id+"F0.wireOp",EDGE,"E209"),sQuery(id+"F0.wireOp",EDGE,"E211"),sQuery(id+"F0.wireOp",EDGE,"E212"),sQuery(id+"F0.wireOp",EDGE,"E213"),sQuery(id+"F0.wireOp",EDGE,"E214"),sQuery(id+"F0.wireOp",EDGE,"E215"),sQuery(id+"F0.wireOp",EDGE,"E217"),sQuery(id+"F0.wireOp",EDGE,"E218"),sQuery(id+"F0.wireOp",EDGE,"E223"),sQuery(id+"F0.wireOp",EDGE,"E224"),sQuery(id+"F0.wireOp",EDGE,"E231")])],"isStart":false});
            var Q7;
            Q7=makeQuery(id+"F0.imprint","IMPRINT",FACE,{"disambiguationData":[TD([[makeQuery(id+"F0.imprint","IMPRINT",EDGE,{"derivedFrom":sQuery(id+"F0.wireOp",EDGE,"E150")}),-1.0]])]});
            var Q8;
            {var subQ1=sQuery(id+"F0.wireOp",EDGE,"E68");Q8=makeQuery(id+"F0.imprint","IMPRINT",FACE,{"disambiguationData":[TD([[makeQuery(id+"F0.imprint","IMPRINT",EDGE,{"derivedFrom":subQ1}),-1.0]])]});}
            extrude(context, id + "F3", {"entities" : qUnion([Q0, Q1, Q2, Q3, Q4, Q5, Q6, Q7, Q8]), "depth" : 2.54 * mm});
        }
        {
            var Q0;
            Q0=qCreatedBy(makeId("Top.planeOp"),FACE);
            var sketch = newSketch(context, id + "F4", { "sketchPlane" : qUnion([Q0])});
            skLineSegment(sketch, "E236", {"start": v(-166.24, -57.37) * mm, "end": v(-154.41, -45.68) * mm});
            skLineSegment(sketch, "E237", {"start": v(-154.41, -45.68) * mm, "end": v(-190.2, -10.55) * mm});
            skLineSegment(sketch, "E238", {"start": v(-190.2, -10.55) * mm, "end": v(-127.02, 51.31) * mm});
            skLineSegment(sketch, "E239", {"start": v(-127.02, 51.31) * mm, "end": v(-127.02, 72.2) * mm});
            skLineSegment(sketch, "E240", {"start": v(-127.02, 72.2) * mm, "end": v(-210.94, -11.72) * mm});
            skLineSegment(sketch, "E241", {"start": v(-210.94, -11.72) * mm, "end": v(-166.24, -57.37) * mm});
            skSolve(sketch);
        }
        {
            var Q0;
            Q0=makeQuery(id+"F4.imprint","IMPRINT",FACE,{"disambiguationData":[TD([[makeQuery(id+"F4.imprint","IMPRINT",EDGE,{"derivedFrom":sQuery(id+"F4.wireOp",EDGE,"E236")}),1.0]])]});
            extrude(context, id + "F5", {"entities" : qUnion([Q0]), "operationType" : NewBodyOperationType.ADD, "depth" : 2.54 * mm});
        }
    });
